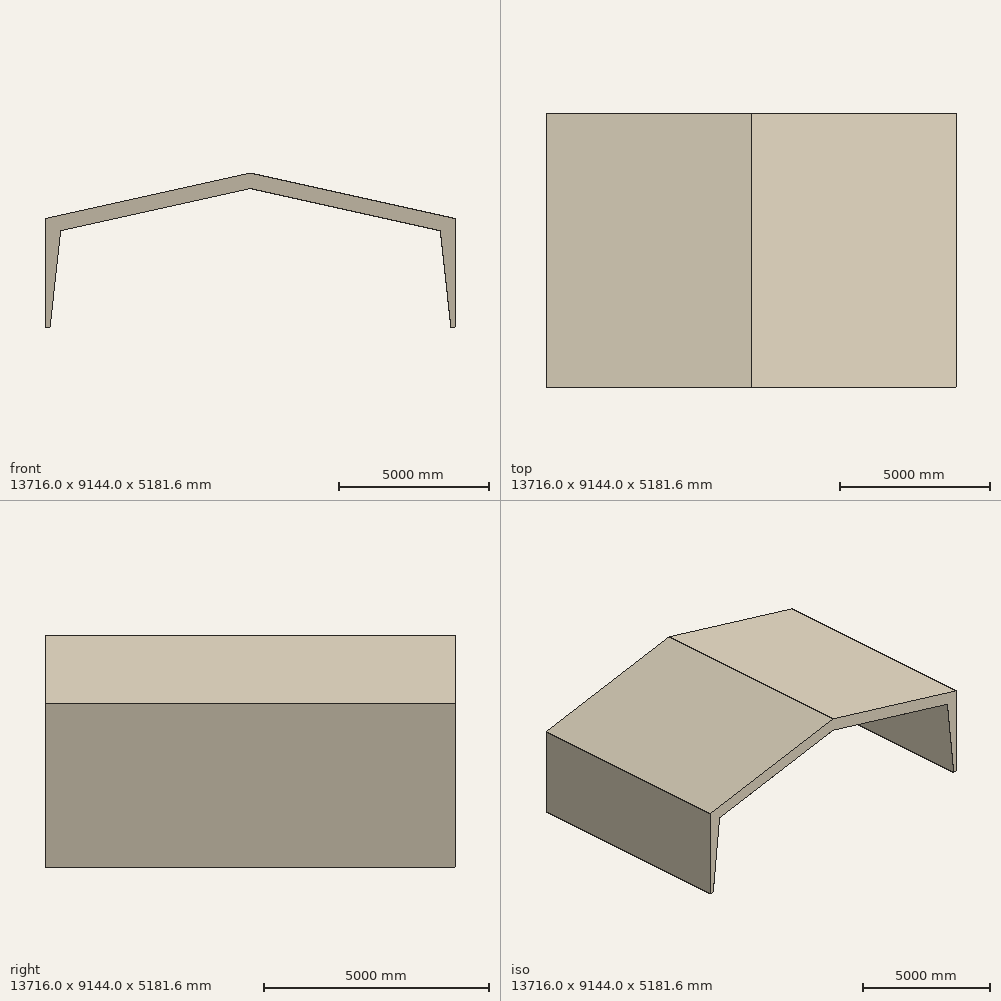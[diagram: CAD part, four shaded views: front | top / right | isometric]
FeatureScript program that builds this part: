
annotation { "Feature Type Name" : "Feature", "Feature Type Description" : "" }
export const myFeature = defineFeature(function(context is Context, id is Id, definition is map)
    precondition{}
    {
        {
            var Q0;
            Q0=qCreatedBy(makeId("Front.planeOp"),FACE);
            var sketch = newSketch(context, id + "F0", { "sketchPlane" : qUnion([Q0])});
            skLineSegment(sketch, "E0", {"start": v(0, 0) * mm, "end": v(0, 3657.6) * mm});
            skLineSegment(sketch, "E1", {"start": v(0, 3657.6) * mm, "end": v(6858, 5181.6) * mm});
            skLineSegment(sketch, "E2", {"start": v(6858, 5181.6) * mm, "end": v(13716, 3657.6) * mm});
            skLineSegment(sketch, "E3", {"start": v(13716, 3657.6) * mm, "end": v(13716, 0) * mm});
            skLineSegment(sketch, "E4", {"start": v(13716, 0) * mm, "end": v(13563.6, 0) * mm});
            skLineSegment(sketch, "E5", {"start": v(13563.6, 0) * mm, "end": v(13208, 3250.1) * mm});
            skLineSegment(sketch, "E6", {"start": v(13208, 3250.1) * mm, "end": v(6858, 4661.2) * mm});
            skLineSegment(sketch, "E7", {"start": v(6858, 4661.2) * mm, "end": v(508, 3250.1) * mm});
            skLineSegment(sketch, "E8", {"start": v(508, 3250.1) * mm, "end": v(152.4, 0) * mm});
            skLineSegment(sketch, "E9", {"start": v(152.4, 0) * mm, "end": v(0, 0) * mm});
            skLineSegment(sketch, "E10", {"start": v(0, 3657.6) * mm, "end": v(13716, 3657.6) * mm, "construction": true});
            skLineSegment(sketch, "E11", {"start": v(6858, 5181.6) * mm, "end": v(6858, 4661.2) * mm, "construction": true});
            skSolve(sketch);
        }
        {
            var Q0;
            Q0 = qSketchRegion(id + "F0", true);
            extrude(context, id + "F1", {"entities" : qUnion([Q0]), "depth" : 30 * 304.8 * mm});
        }
    });
